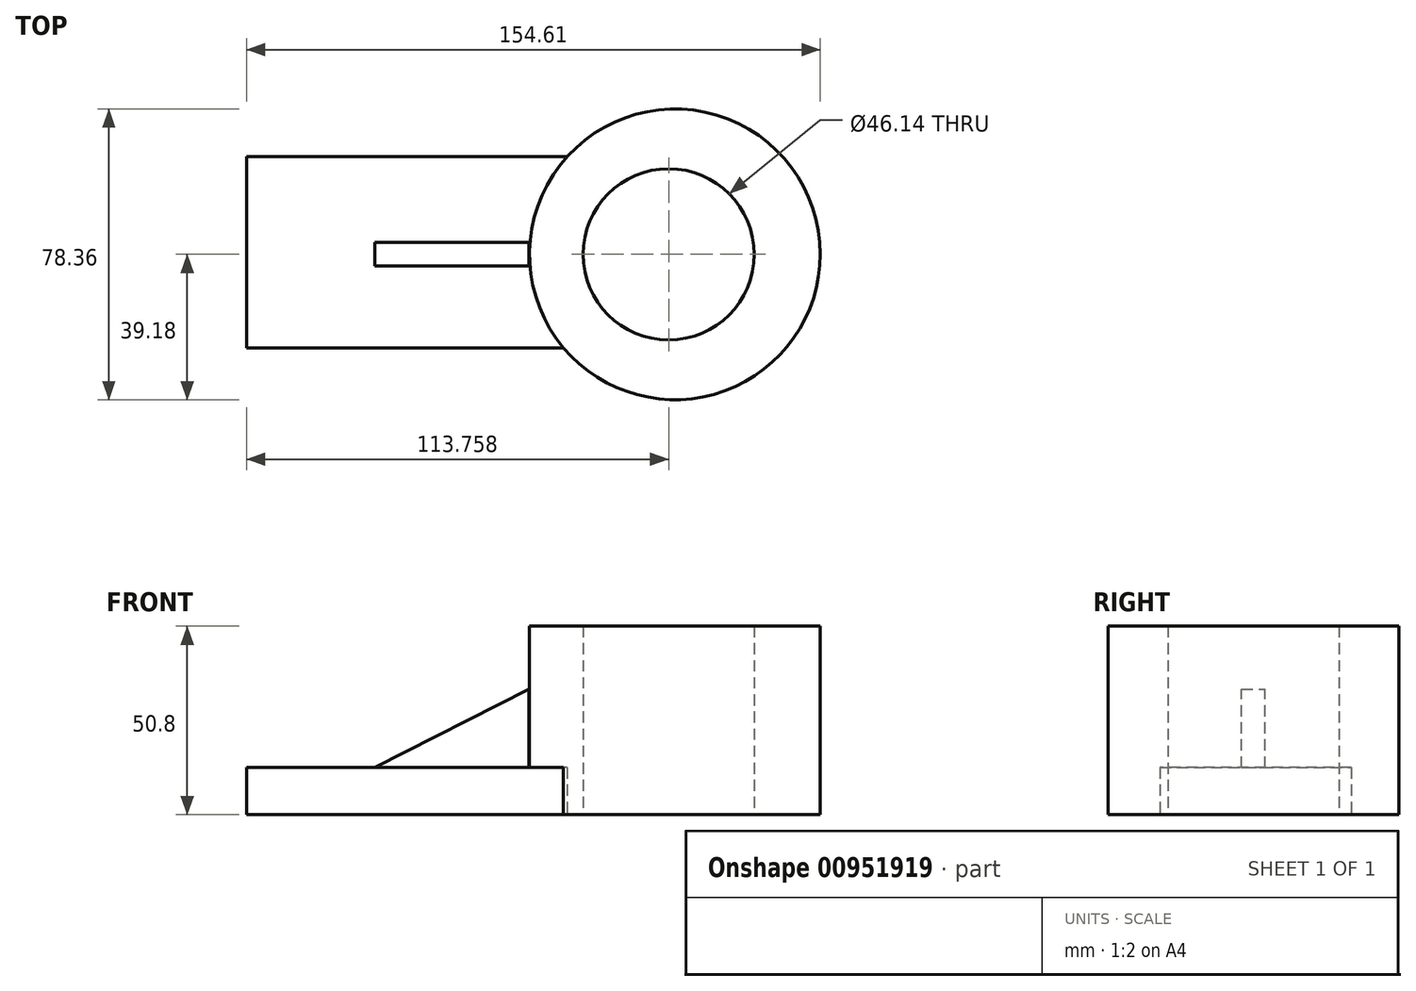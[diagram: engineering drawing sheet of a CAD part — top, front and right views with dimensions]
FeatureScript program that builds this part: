
annotation { "Feature Type Name" : "Feature", "Feature Type Description" : "" }
export const myFeature = defineFeature(function(context is Context, id is Id, definition is map)
    precondition{}
    {
        {
            var Q0;
            Q0=qCreatedBy(makeId("Top.planeOp"),FACE);
            var sketch = newSketch(context, id + "F0", { "sketchPlane" : qUnion([Q0])});
            skCircle(sketch, "E0", {"center": v(39.29, 0) * mm, "radius": 39.18 * mm});
            skLineSegment(sketch, "E1.bottom", {"start": v(-75.84, -31.75) * mm, "end": v(29.5, -31.75) * mm});
            skLineSegment(sketch, "E1.top", {"start": v(-75.84, 31.75) * mm, "end": v(29.5, 31.75) * mm});
            skLineSegment(sketch, "E1.left", {"start": v(-75.84, -31.75) * mm, "end": v(-75.84, 31.75) * mm});
            skLineSegment(sketch, "E1.right", {"start": v(29.5, -31.75) * mm, "end": v(29.5, 31.75) * mm});
            skSolve(sketch);
        }
        {
            var Q0;
            {var subQ5=sQuery(id+"F0.wireOp",EDGE,"E1.right");Q0=makeQuery(id+"F0.imprint","IMPRINT",FACE,{"disambiguationData":[TD([[makeQuery(id+"F0.imprint","IMPRINT",EDGE,{"derivedFrom":subQ5}),-1.0]])]});}
            var Q1;
            {var subQ5=sQuery(id+"F0.wireOp",EDGE,"E1.right");Q1=makeQuery(id+"F0.imprint","IMPRINT",FACE,{"disambiguationData":[TD([[makeQuery(id+"F0.imprint","IMPRINT",EDGE,{"derivedFrom":subQ5}),1.0]])]});}
            extrude(context, id + "F1", {"entities" : qUnion([Q0, Q1]), "depth" : 50.8 * mm, "offsetDistance" : 25.4 * mm});
        }
        {
            var Q0;
            Q0=qCreatedBy(makeId("Top.planeOp"),FACE);
            var sketch = newSketch(context, id + "F2", { "sketchPlane" : qUnion([Q0])});
            skCircle(sketch, "E2", {"center": v(37.6, 0) * mm, "radius": 23.07 * mm});
            skSolve(sketch);
        }
        {
            var Q0;
            Q0 = qSketchRegion(id + "F2", true);
            extrude(context, id + "F3", {"entities" : qUnion([Q0]), "operationType" : NewBodyOperationType.REMOVE, "depth" : 130.05 * mm, "offsetDistance" : 25.4 * mm});
        }
        {
            var Q0;
            Q0=qCreatedBy(makeId("Top.planeOp"),FACE);
            var sketch = newSketch(context, id + "F4", { "sketchPlane" : qUnion([Q0])});
            skLineSegment(sketch, "E3.bottom", {"start": v(-76.15, -25.18) * mm, "end": v(12.79, -25.18) * mm});
            skLineSegment(sketch, "E3.top", {"start": v(-76.15, 26.33) * mm, "end": v(12.79, 26.33) * mm});
            skLineSegment(sketch, "E3.left", {"start": v(-76.15, -25.18) * mm, "end": v(-76.15, 26.33) * mm});
            skLineSegment(sketch, "E3.right", {"start": v(12.79, -25.18) * mm, "end": v(12.79, 26.33) * mm});
            skSolve(sketch);
        }
        {
            var Q0;
            Q0=makeQuery(id+"F4.imprint","IMPRINT",FACE,{"disambiguationData":[TD([[makeQuery(id+"F4.imprint","IMPRINT",EDGE,{"derivedFrom":sQuery(id+"F4.wireOp",EDGE,"E3.bottom")}),1.0]])]});
            extrude(context, id + "F5", {"entities" : qUnion([Q0]), "operationType" : NewBodyOperationType.ADD, "depth" : 12.7 * mm, "offsetDistance" : 25.4 * mm});
        }
        {
            var Q0;
            Q0=qCreatedBy(makeId("Front.planeOp"),FACE);
            var sketch = newSketch(context, id + "F6", { "sketchPlane" : qUnion([Q0])});
            skLineSegment(sketch, "E4", {"start": v(0, 33.82) * mm, "end": v(-66.65, 0) * mm});
            skLineSegment(sketch, "E5", {"start": v(-66.65, 0) * mm, "end": v(0, 0) * mm});
            skLineSegment(sketch, "E6", {"start": v(0, 0) * mm, "end": v(0, 33.82) * mm});
            skSolve(sketch);
        }
        {
            var Q0;
            Q0 = qSketchRegion(id + "F6", true);
            extrude(context, id + "F7", {"entities" : qUnion([Q0]), "operationType" : NewBodyOperationType.ADD, "depth" : 6.35 * mm, "offsetDistance" : 25.4 * mm, "symmetric" : true});
        }
    });
